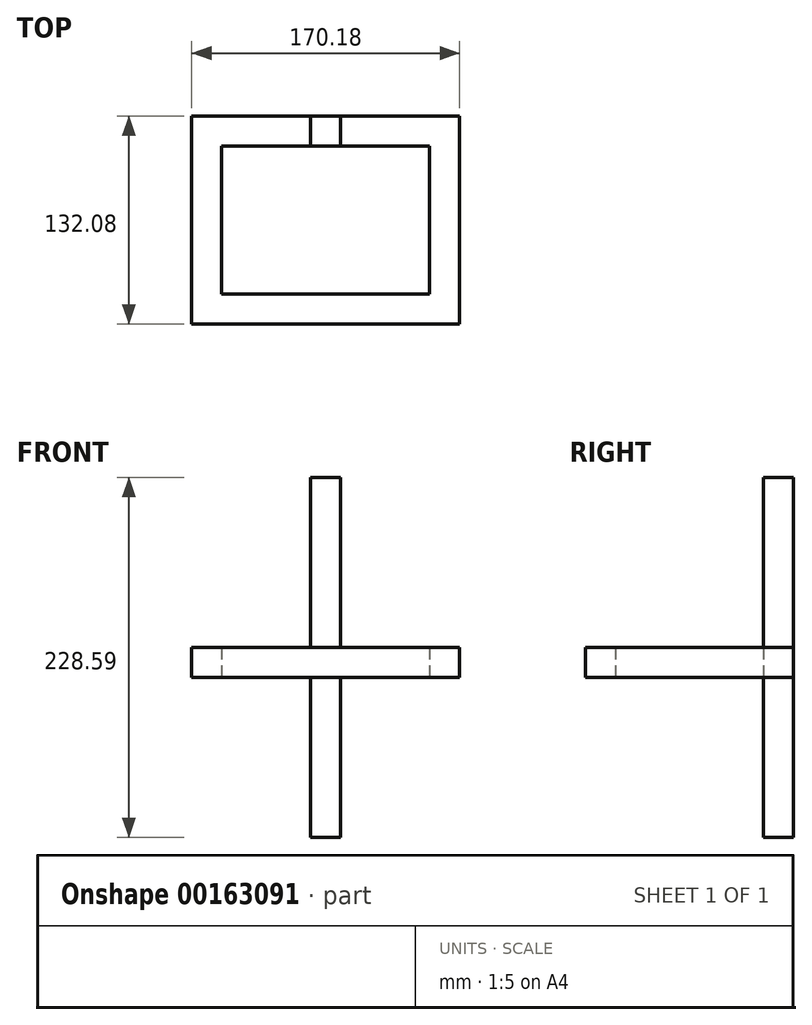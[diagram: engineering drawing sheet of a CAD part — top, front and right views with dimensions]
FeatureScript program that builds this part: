
annotation { "Feature Type Name" : "Feature", "Feature Type Description" : "" }
export const myFeature = defineFeature(function(context is Context, id is Id, definition is map)
    precondition{}
    {
        {
            var Q0;
            Q0=qCreatedBy(makeId("Top.planeOp"),FACE);
            var sketch = newSketch(context, id + "F0", { "sketchPlane" : qUnion([Q0])});
            skLineSegment(sketch, "E0.bottom", {"start": v(66.04, 46.99) * mm, "end": v(-66.04, 46.99) * mm});
            skLineSegment(sketch, "E0.top", {"start": v(66.04, -47) * mm, "end": v(-66.04, -47) * mm});
            skLineSegment(sketch, "E0.left", {"start": v(66.04, 47) * mm, "end": v(66.04, -47) * mm});
            skLineSegment(sketch, "E0.right", {"start": v(-66.04, 47) * mm, "end": v(-66.04, -47) * mm});
            skPoint(sketch, "E0.middle", {"position": v(0, 0) * mm});
            skLineSegment(sketch, "E1.bottom", {"start": v(-85.1, 66.04) * mm, "end": v(85.1, 66.04) * mm});
            skLineSegment(sketch, "E1.top", {"start": v(-85.1, -66.04) * mm, "end": v(85.1, -66.04) * mm});
            skLineSegment(sketch, "E1.left", {"start": v(-85.1, 66.04) * mm, "end": v(-85.1, -66.04) * mm});
            skLineSegment(sketch, "E1.right", {"start": v(85.1, 66.04) * mm, "end": v(85.1, -66.04) * mm});
            skSolve(sketch);
        }
        {
            var Q0;
            Q0=makeQuery(id+"F0.imprint","IMPRINT",FACE,{"disambiguationData":[TD([[makeQuery(id+"F0.imprint","IMPRINT",EDGE,{"derivedFrom":sQuery(id+"F0.wireOp",EDGE,"E0.bottom")}),-1.0]])]});
            extrude(context, id + "F1", {"entities" : qUnion([Q0]), "endBound" : BoundingType.SYMMETRIC, "depth" : 19.05 * mm});
        }
        {
            var Q0;
            Q0=makeQuery(id+"F1.opExtrude","CAP_FACE",FACE,{"disambiguationData":[OSD([sQuery(id+"F0.wireOp",EDGE,"E0.bottom"),sQuery(id+"F0.wireOp",EDGE,"E0.top"),sQuery(id+"F0.wireOp",EDGE,"E0.left"),sQuery(id+"F0.wireOp",EDGE,"E0.right"),sQuery(id+"F0.wireOp",EDGE,"E1.bottom"),sQuery(id+"F0.wireOp",EDGE,"E1.top"),sQuery(id+"F0.wireOp",EDGE,"E1.left"),sQuery(id+"F0.wireOp",EDGE,"E1.right")])],"isStart":true});
            var sketch = newSketch(context, id + "F2", { "sketchPlane" : qUnion([Q0])});
            skLineSegment(sketch, "E2.bottom", {"start": v(-9.52, -46.99) * mm, "end": v(9.52, -46.99) * mm});
            skLineSegment(sketch, "E2.top", {"start": v(-9.52, -66.04) * mm, "end": v(9.52, -66.04) * mm});
            skLineSegment(sketch, "E2.left", {"start": v(-9.52, -47) * mm, "end": v(-9.52, -66.04) * mm});
            skLineSegment(sketch, "E2.right", {"start": v(9.53, -46.99) * mm, "end": v(9.53, -66.04) * mm});
            skPoint(sketch, "E3", {"position": v(0, -66.04) * mm});
            skSolve(sketch);
        }
        {
            var Q0;
            Q0 = qSketchRegion(id + "F2", true);
            extrude(context, id + "F3", {"entities" : qUnion([Q0]), "operationType" : NewBodyOperationType.ADD, "depth" : 101.6 * mm, "hasSecondDirection" : true, "secondDirectionOppositeDirection" : true, "secondDirectionDepth" : 127 * mm});
        }
    });
